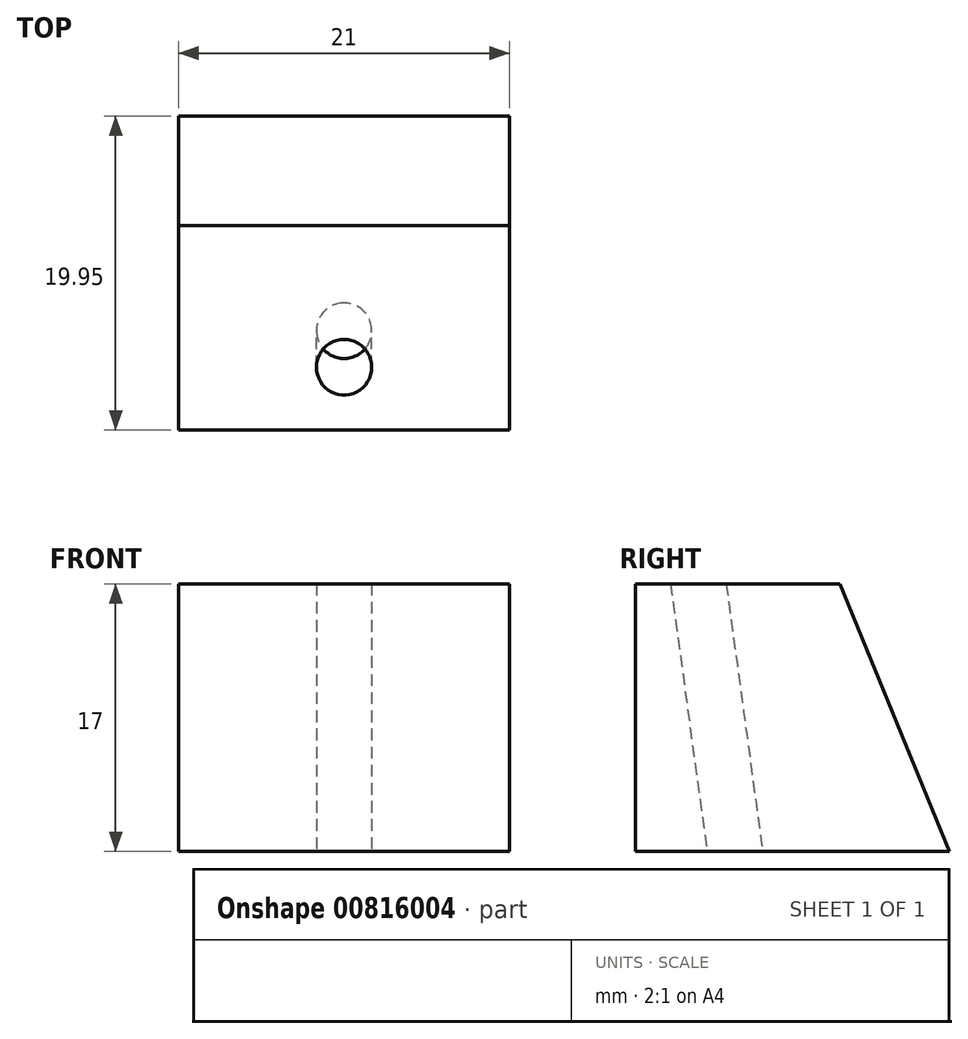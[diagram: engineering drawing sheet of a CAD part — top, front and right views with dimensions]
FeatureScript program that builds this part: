
annotation { "Feature Type Name" : "Feature", "Feature Type Description" : "" }
export const myFeature = defineFeature(function(context is Context, id is Id, definition is map)
    precondition{}
    {
        {
            var Q0;
            Q0=qCreatedBy(makeId("Right.planeOp"),FACE);
            var sketch = newSketch(context, id + "F0", { "sketchPlane" : qUnion([Q0])});
            skLineSegment(sketch, "E0", {"start": v(0, 0) * mm, "end": v(22, 0) * mm});
            skLineSegment(sketch, "E1", {"start": v(22, 0) * mm, "end": v(13, 22) * mm});
            skLineSegment(sketch, "E2", {"start": v(13, 22) * mm, "end": v(0, 22) * mm});
            skLineSegment(sketch, "E3", {"start": v(0, 22) * mm, "end": v(0, 0) * mm});
            skSolve(sketch);
        }
        {
            var Q0;
            Q0 = qSketchRegion(id + "F0", true);
            extrude(context, id + "F1", {"entities" : qUnion([Q0]), "depth" : 21 * mm, "offsetDistance" : 25 * mm});
        }
        {
            var Q0;
            Q0=qCreatedBy(makeId("Top.planeOp"),FACE);
            var sketch = newSketch(context, id + "F2", { "sketchPlane" : qUnion([Q0])});
            skCircle(sketch, "E4", {"center": v(10.5, 7) * mm, "radius": 1.75 * mm});
            skSolve(sketch);
        }
        {
            var Q0;
            Q0=qCreatedBy(makeId("Right.planeOp"),FACE);
            var sketch = newSketch(context, id + "F3", { "sketchPlane" : qUnion([Q0])});
            skPoint(sketch, "E5", {"position": v(4, 22) * mm});
            skPoint(sketch, "E6", {"position": v(7, 0) * mm});
            skLineSegment(sketch, "E7", {"start": v(4, 22) * mm, "end": v(7, 0) * mm});
            skLineSegment(sketch, "E8", {"start": v(7, 0) * mm, "end": v(7, 0) * mm});
            skSolve(sketch);
        }
        {
            var Q0;
            Q0=sQuery(id+"F3.wireOp",EDGE,"E7");
            cPlane(context, id + "F4", {"entities" : qUnion([Q0]), "cplaneType" : CPlaneType.MID_PLANE, "offset" : 25 * mm, "width" : 150 * mm, "height" : 150 * mm});
        }
        {
            var Q0;
            Q0=qCreatedBy(id+"F4.planeOp",FACE);
            var sketch = newSketch(context, id + "F5", { "sketchPlane" : qUnion([Q0])});
            skCircle(sketch, "E9", {"center": v(10.5, -6.94) * mm, "radius": 1.75 * mm});
            skLineSegment(sketch, "E10", {"start": v(0, -6.94) * mm, "end": v(10.5, -6.94) * mm});
            skSolve(sketch);
        }
        {
            var Q0;
            Q0 = qSketchRegion(id + "F5", true);
            extrude(context, id + "F6", {"entities" : qUnion([Q0]), "operationType" : NewBodyOperationType.REMOVE, "endBound" : BoundingType.THROUGH_ALL, "oppositeDirection" : true, "depth" : 25 * mm, "offsetDistance" : 25 * mm, "hasSecondDirection" : true, "secondDirectionBound" : SecondDirectionBoundingType.THROUGH_ALL, "secondDirectionOppositeDirection" : false, "secondDirectionDepth" : 25 * mm});
        }
        {
            var Q0;
            Q0=qCreatedBy(makeId("Right.planeOp"),FACE);
            var sketch = newSketch(context, id + "F7", { "sketchPlane" : qUnion([Q0])});
            skLineSegment(sketch, "E11.bottom", {"start": v(0, 0) * mm, "end": v(22, 0) * mm});
            skLineSegment(sketch, "E11.top", {"start": v(0, 5) * mm, "end": v(22, 5) * mm});
            skLineSegment(sketch, "E11.left", {"start": v(0, 0) * mm, "end": v(0, 5) * mm});
            skLineSegment(sketch, "E11.right", {"start": v(22, 0) * mm, "end": v(22, 5) * mm});
            skSolve(sketch);
        }
        {
            var Q0;
            Q0 = qSketchRegion(id + "F7", true);
            extrude(context, id + "F8", {"entities" : qUnion([Q0]), "operationType" : NewBodyOperationType.REMOVE, "endBound" : BoundingType.THROUGH_ALL, "depth" : 25 * mm, "offsetDistance" : 25 * mm});
        }
        {
            var Q0;
            Q0=makeQuery(id+"F1.opExtrude","SWEPT_BODY",BODY,{"disambiguationData":[OSD([sQuery(id+"F0.wireOp",EDGE,"E0"),sQuery(id+"F0.wireOp",EDGE,"E1"),sQuery(id+"F0.wireOp",EDGE,"E2"),sQuery(id+"F0.wireOp",EDGE,"E3")])]});
            transform(context, id + "F9", {"entities" : qUnion([Q0]), "transformType" : TransformType.TRANSLATION_3D, "dx" : 0 * mm, "dy" : 0 * mm, "dz" : -5 * mm, "makeCopy" : false});
        }
    });
